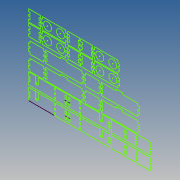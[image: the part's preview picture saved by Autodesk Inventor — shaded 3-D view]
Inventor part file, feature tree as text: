
AUTODESK INVENTOR PART (.ipt)
format: ipt  version: 2020 (Build 240168000, 168)  size: 242,176 bytes
history: native  units: mm
features: sketch x1
ambient origin geometry x8: Origin, YZ Plane, XZ Plane, XY Plane, X Axis, Y Axis, Z Axis, Center Point
feature tree (1):
  sketch  "Sketch1"
